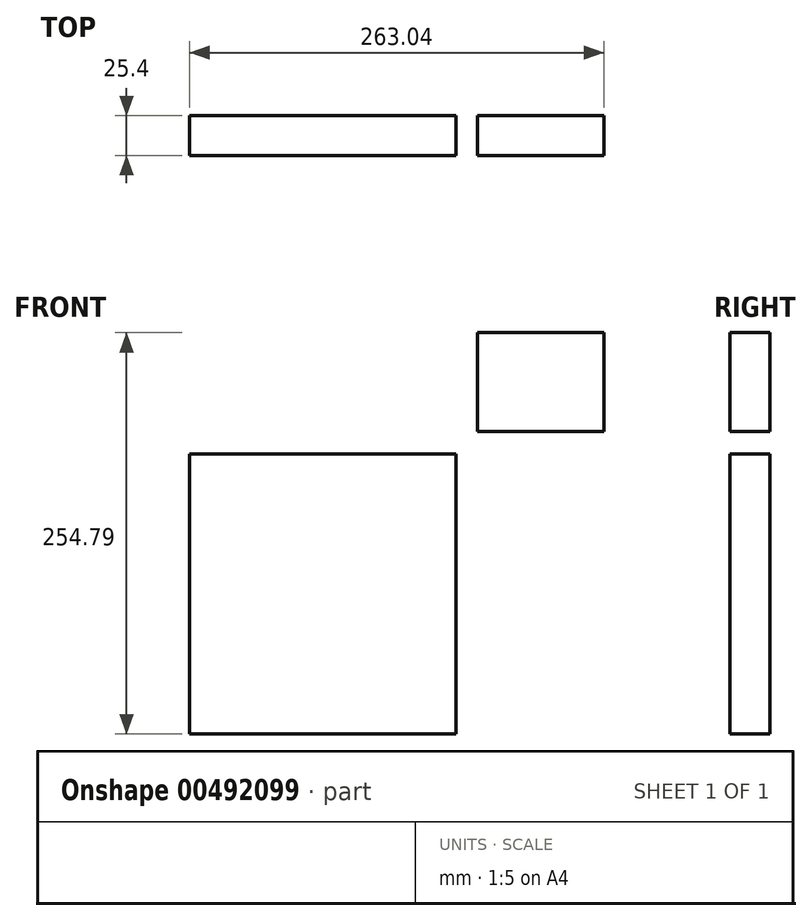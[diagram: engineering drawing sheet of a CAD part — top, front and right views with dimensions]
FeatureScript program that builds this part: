
annotation { "Feature Type Name" : "Feature", "Feature Type Description" : "" }
export const myFeature = defineFeature(function(context is Context, id is Id, definition is map)
    precondition{}
    {
        {
            var Q0;
            Q0=qCreatedBy(makeId("Front.planeOp"),FACE);
            var sketch = newSketch(context, id + "F0", { "sketchPlane" : qUnion([Q0])});
            skLineSegment(sketch, "E0.bottom", {"start": v(-80.22, 54.34) * mm, "end": v(0, 54.34) * mm});
            skLineSegment(sketch, "E0.top", {"start": v(-80.22, -8.53) * mm, "end": v(0, -8.53) * mm});
            skLineSegment(sketch, "E0.left", {"start": v(-80.22, 54.34) * mm, "end": v(-80.22, -8.53) * mm});
            skLineSegment(sketch, "E0.right", {"start": v(0, 54.34) * mm, "end": v(0, -8.53) * mm});
            skSolve(sketch);
        }
        {
            var Q0;
            Q0=qCreatedBy(makeId("Front.planeOp"),FACE);
            var sketch = newSketch(context, id + "F1", { "sketchPlane" : qUnion([Q0])});
            skLineSegment(sketch, "E1.bottom", {"start": v(-263.04, -22.71) * mm, "end": v(-93.88, -22.71) * mm});
            skLineSegment(sketch, "E1.top", {"start": v(-263.04, -200.45) * mm, "end": v(-93.88, -200.45) * mm});
            skLineSegment(sketch, "E1.left", {"start": v(-263.04, -22.71) * mm, "end": v(-263.04, -200.45) * mm});
            skLineSegment(sketch, "E1.right", {"start": v(-93.88, -22.71) * mm, "end": v(-93.88, -200.45) * mm});
            skSolve(sketch);
        }
        {
            var Q0;
            Q0=makeQuery(id+"F1.imprint","IMPRINT",FACE,{"disambiguationData":[TD([[makeQuery(id+"F1.imprint","IMPRINT",EDGE,{"derivedFrom":sQuery(id+"F1.wireOp",EDGE,"E1.bottom")}),-1.0]])]});
            var Q1;
            Q1=makeQuery(id+"F0.imprint","IMPRINT",FACE,{"disambiguationData":[TD([[makeQuery(id+"F0.imprint","IMPRINT",EDGE,{"derivedFrom":sQuery(id+"F0.wireOp",EDGE,"E0.bottom")}),-1.0]])]});
            extrude(context, id + "F2", {"entities" : qUnion([Q0, Q1]), "depth" : 25.4 * mm});
        }
    });
